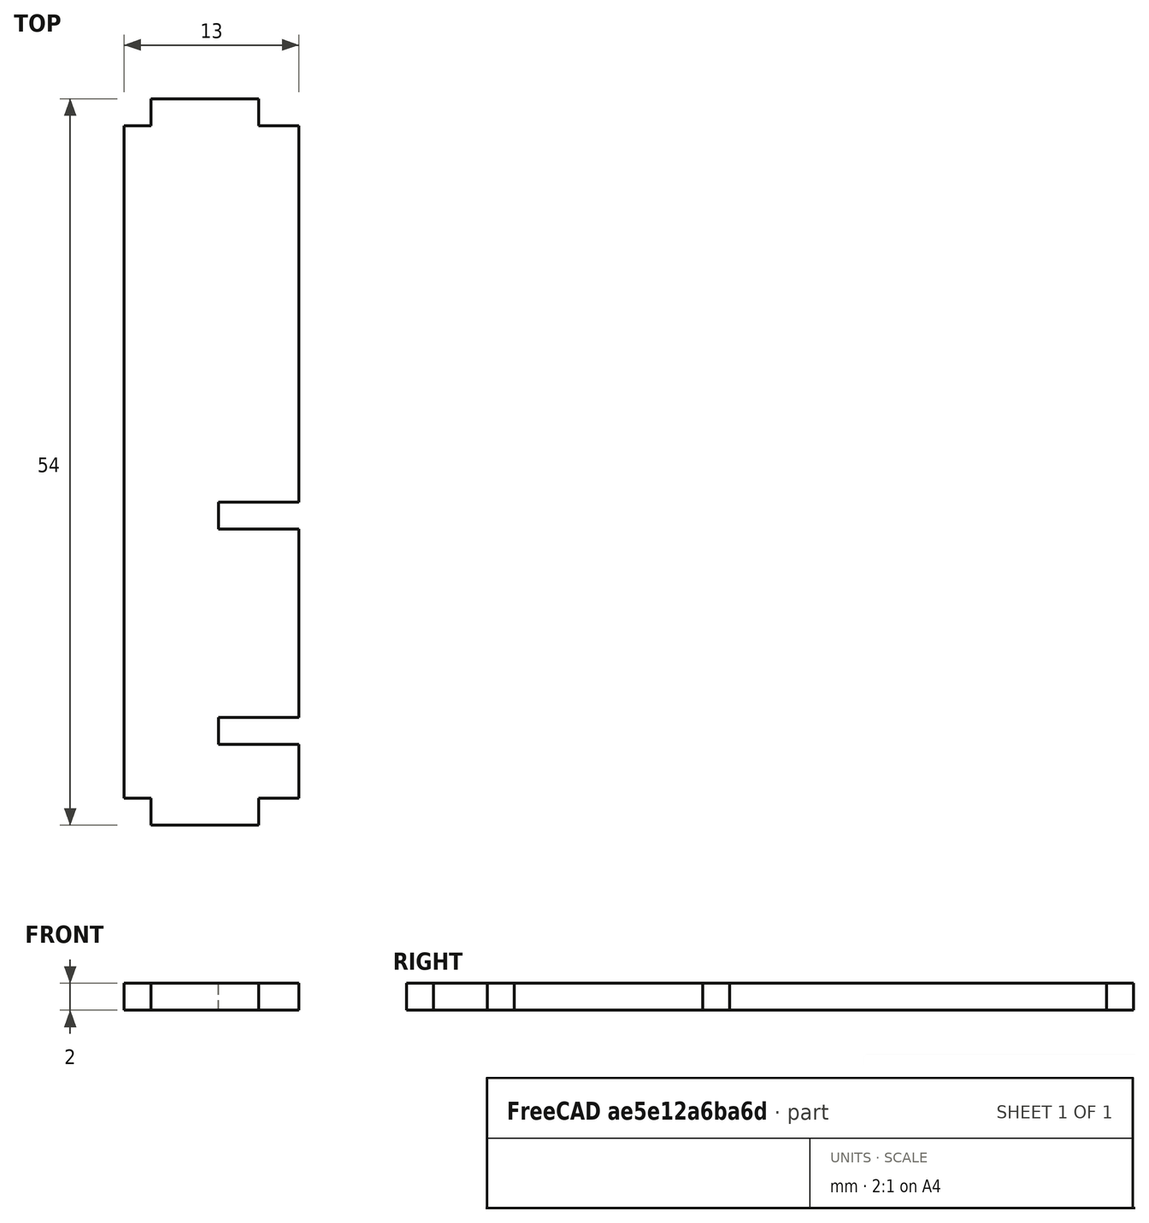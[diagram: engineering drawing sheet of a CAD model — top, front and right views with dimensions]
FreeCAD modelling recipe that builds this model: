
FCSTD DOCUMENT  (FreeCAD 0.18R16131 (Git))
Label: renforts_11
License: All rights reserved
LicenseURL: http://en.wikipedia.org/wiki/All_rights_reserved
objects: Sketcher::SketchObject×1, PartDesign::Pad×1, PartDesign::Body×1
note: 4 computed .brp shape members not serialized (recipe doc carries the construction recipe); baked Part::Feature solids carry a one-line shape summary decoded from their .brp

FEATURE [Sketcher::SketchObject] Sketch
  MapMode = 5
  Support = -> [XY_Plane]
  sketch-geometry (20):
    g0: LineSegment StartX=0 StartY=52 StartZ=0 EndX=2 EndY=52 EndZ=0
    g1: LineSegment StartX=2 StartY=52 StartZ=0 EndX=2 EndY=54 EndZ=0
    g2: LineSegment StartX=2 StartY=54 StartZ=0 EndX=10 EndY=54 EndZ=0
    g3: LineSegment StartX=10 StartY=54 StartZ=0 EndX=10 EndY=52 EndZ=0
    g4: LineSegment StartX=10 StartY=52 StartZ=0 EndX=13 EndY=52 EndZ=0
    g5: LineSegment StartX=13 StartY=52 StartZ=0 EndX=13 EndY=24 EndZ=0
    g6: LineSegment StartX=13 StartY=24 StartZ=0 EndX=7 EndY=24 EndZ=0
    g7: LineSegment StartX=7 StartY=24 StartZ=0 EndX=7 EndY=22 EndZ=0
    g8: LineSegment StartX=7 StartY=22 StartZ=0 EndX=13 EndY=22 EndZ=0
    g9: LineSegment StartX=13 StartY=2 StartZ=0 EndX=10 EndY=2 EndZ=0
    g10: LineSegment StartX=10 StartY=2 StartZ=0 EndX=10 EndY=0 EndZ=0
    g11: LineSegment StartX=10 StartY=0 StartZ=0 EndX=2 EndY=0 EndZ=0
    g12: LineSegment StartX=2 StartY=0 StartZ=0 EndX=2 EndY=2 EndZ=0
    g13: LineSegment StartX=2 StartY=2 StartZ=0 EndX=0 EndY=2 EndZ=0
    g14: LineSegment StartX=0 StartY=2 StartZ=0 EndX=0 EndY=52 EndZ=0
    g15: LineSegment StartX=13 StartY=2 StartZ=0 EndX=13 EndY=6 EndZ=0
    g16: LineSegment StartX=13 StartY=6 StartZ=0 EndX=7 EndY=6 EndZ=0
    g17: LineSegment StartX=7 StartY=6 StartZ=0 EndX=7 EndY=8 EndZ=0
    g18: LineSegment StartX=7 StartY=8 StartZ=0 EndX=13 EndY=8 EndZ=0
    g19: LineSegment StartX=13 StartY=8 StartZ=0 EndX=13 EndY=22 EndZ=0
  constraints (60):
    c: Coincident(g0,g1)
    c: Coincident(g1,g2)
    c: Coincident(g2,g3)
    c: Coincident(g3,g4)
    c: Coincident(g4,g5)
    c: Coincident(g5,g6)
    c: Coincident(g6,g7)
    c: Coincident(g7,g8)
    c: Coincident(g9,g10)
    c: Coincident(g10,g11)
    c: Coincident(g11,g12)
    c: Coincident(g12,g13)
    c: Coincident(g13,g14)
    c: Coincident(g14,g0)
    c: Vertical(g5)
    c: Vertical(g7)
    c: Vertical(g10)
    c: Vertical(g12)
    c: Vertical(g14)
    c: Vertical(g1)
    c: Vertical(g3)
    c: Horizontal(g2)
    c: Horizontal(g0)
    c: Horizontal(g4)
    c: Horizontal(g6)
    c: Horizontal(g8)
    c: Horizontal(g9)
    c: Horizontal(g11)
    c: Horizontal(g13)
    c: PointOnObject(g13,g-2)
    c: PointOnObject(g11,g-1)
    c: Vertical(g8,g5)
    c: DistanceX(g-1,g9) = 13
    c: DistanceX(g6,g6) = 6
    c: DistanceY(g9,g8) = 20
    c: DistanceY(g7,g7) = 2
    c: Equal(g3,g1)
    c: Equal(g1,g7)
    c: Equal(g7,g12)
    c: Vertical(g11,g0)
    c: DistanceX(g13,g13) = 2
    c: DistanceX(g11,g11) = 8
    c: Equal(g11,g2)
    c: Equal(g12,g10)
    c: DistanceY(g14,g14) = 50
    c: Coincident(g15,g16)
    c: Coincident(g16,g17)
    c: Coincident(g17,g18)
    c: Coincident(g18,g19)
    c: Coincident(g19,g8)
    c: Coincident(g9,g15)
    c: Vertical(g19)
    c: Vertical(g15)
    c: Vertical(g17)
    c: Horizontal(g18)
    c: Horizontal(g16)
    c: Equal(g7,g17)
    c: DistanceY(g15,g15) = 4
    c: Equal(g18,g8)
    c: Vertical(g18,g15)
FEATURE [PartDesign::Pad] Pad
  Length = 2
  Length2 = 100
  Profile = -> Sketch
  Type = 0
FEATURE [PartDesign::Body] Body
  Group = -> [Sketch,Pad]
  Origin = -> Origin
  Tip = -> Pad
